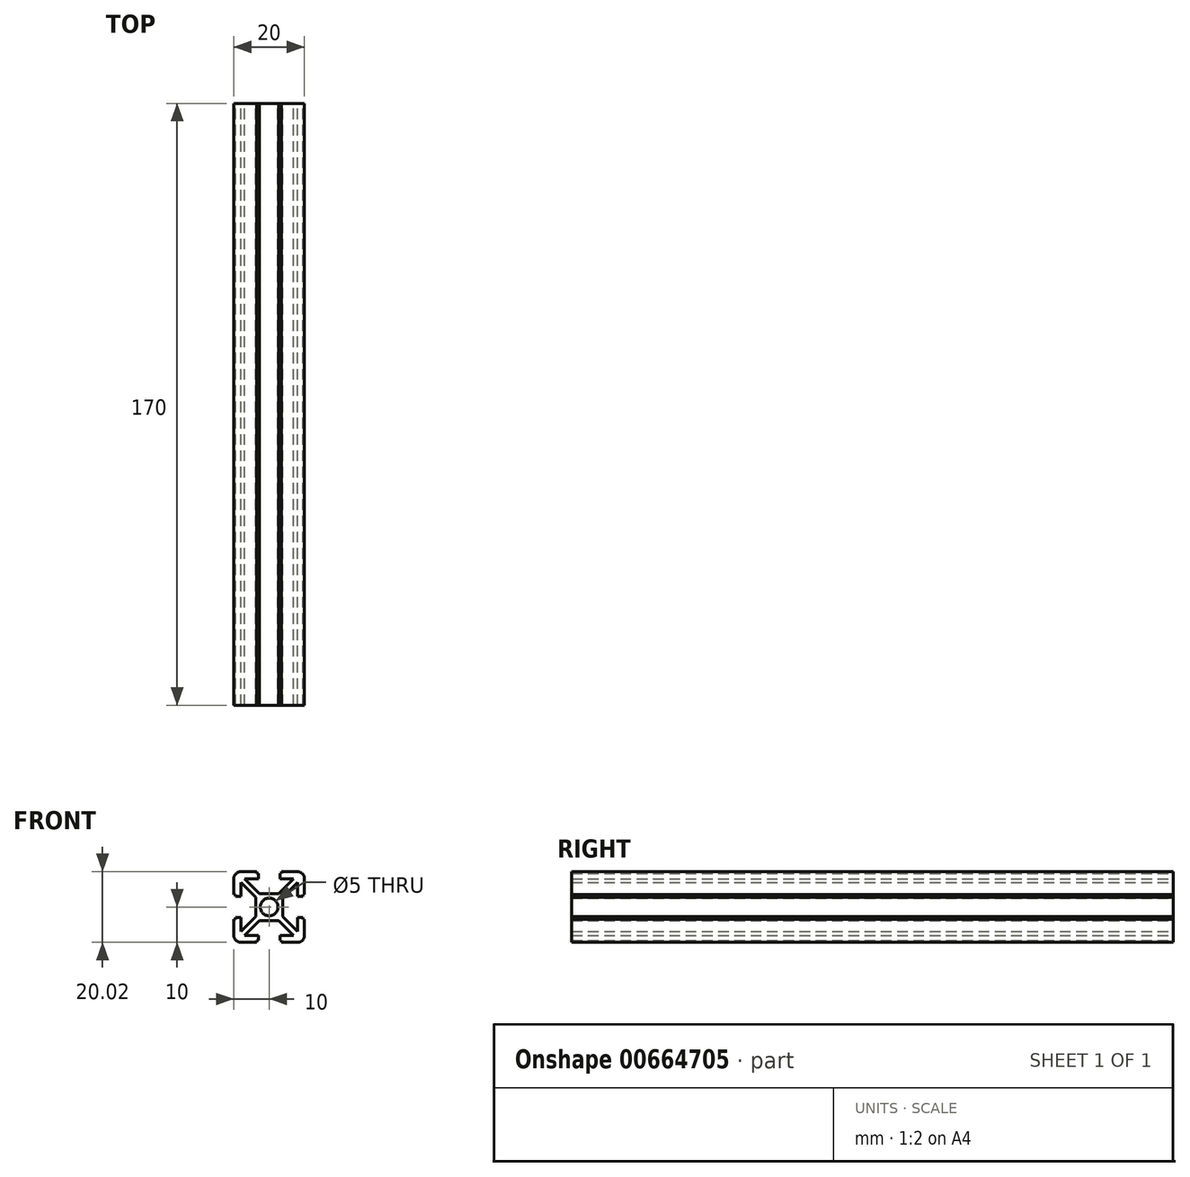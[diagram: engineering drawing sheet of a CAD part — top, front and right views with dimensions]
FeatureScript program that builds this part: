
annotation { "Feature Type Name" : "Feature", "Feature Type Description" : "" }
export const myFeature = defineFeature(function(context is Context, id is Id, definition is map)
    precondition{}
    {
        {
            var Q0;
            Q0=qCreatedBy(makeId("Front.planeOp"),FACE);
            var sketch = newSketch(context, id + "F0", { "sketchPlane" : qUnion([Q0])});
            skPoint(sketch, "E0.middle", {"position": v(10, -10) * mm});
            skPoint(sketch, "E1.visualSharp", {"position": v(0, 0) * mm});
            skArc(sketch, "E1.filletArc", {"start": v(2, 0) * mm, "mid": v(0.59, -0.59) * mm, "end": v(0, -2) * mm});
            skPoint(sketch, "E2.visualSharp", {"position": v(20, 0) * mm});
            skArc(sketch, "E2.filletArc", {"start": v(20, -2) * mm, "mid": v(19.41, -0.59) * mm, "end": v(18, 0) * mm});
            skPoint(sketch, "E3.visualSharp", {"position": v(20, -20) * mm});
            skArc(sketch, "E3.filletArc", {"start": v(18, -20) * mm, "mid": v(19.41, -19.41) * mm, "end": v(20, -18) * mm});
            skArc(sketch, "E4.filletArc", {"start": v(0, -18) * mm, "mid": v(0.59, -19.41) * mm, "end": v(2, -20) * mm});
            skLineSegment(sketch, "E5", {"start": v(2, 0) * mm, "end": v(6.5, 0) * mm});
            skLineSegment(sketch, "E6", {"start": v(6.5, 0) * mm, "end": v(6.5, -0.5) * mm});
            skLineSegment(sketch, "E7", {"start": v(13.02, -0.5) * mm, "end": v(13.5, -0.5) * mm});
            skLineSegment(sketch, "E8", {"start": v(13.5, 0.02) * mm, "end": v(18, 0) * mm});
            skLineSegment(sketch, "E9", {"start": v(20, -2) * mm, "end": v(20, -6.5) * mm});
            skLineSegment(sketch, "E10", {"start": v(20, -6.5) * mm, "end": v(19.5, -6.5) * mm});
            skLineSegment(sketch, "E11", {"start": v(19.5, -6.5) * mm, "end": v(19.5, -7) * mm});
            skLineSegment(sketch, "E12", {"start": v(13.83, -7.25) * mm, "end": v(13.83, -12.77) * mm});
            skLineSegment(sketch, "E13", {"start": v(19.53, -12.98) * mm, "end": v(19.54, -13.46) * mm});
            skLineSegment(sketch, "E14", {"start": v(20, -13.46) * mm, "end": v(20, -18) * mm});
            skLineSegment(sketch, "E15", {"start": v(18, -20) * mm, "end": v(13.5, -20) * mm});
            skLineSegment(sketch, "E16", {"start": v(13.5, -20) * mm, "end": v(13.5, -19.5) * mm});
            skLineSegment(sketch, "E17", {"start": v(12.74, -13.8) * mm, "end": v(7.26, -13.8) * mm});
            skLineSegment(sketch, "E18", {"start": v(7, -19.5) * mm, "end": v(6.5, -19.5) * mm});
            skLineSegment(sketch, "E19", {"start": v(6.5, -19.5) * mm, "end": v(6.5, -20) * mm});
            skLineSegment(sketch, "E20", {"start": v(6.5, -20) * mm, "end": v(2, -20) * mm});
            skLineSegment(sketch, "E21", {"start": v(0, -18) * mm, "end": v(0, -13.5) * mm});
            skLineSegment(sketch, "E22", {"start": v(6.2, -12.74) * mm, "end": v(6.2, -7.26) * mm});
            skLineSegment(sketch, "E23", {"start": v(0, -6.49) * mm, "end": v(0, -2) * mm});
            skLineSegment(sketch, "E24", {"start": v(7, -19.5) * mm, "end": v(7, -18) * mm});
            skLineSegment(sketch, "E25", {"start": v(13.02, -19.5) * mm, "end": v(13.02, -18) * mm});
            skLineSegment(sketch, "E26", {"start": v(13.02, -18) * mm, "end": v(16.94, -18) * mm});
            skLineSegment(sketch, "E27", {"start": v(7, -0.5) * mm, "end": v(7, -2) * mm});
            skLineSegment(sketch, "E28", {"start": v(7, -2) * mm, "end": v(3.06, -2) * mm});
            skLineSegment(sketch, "E29", {"start": v(3.06, -2) * mm, "end": v(7.26, -6.2) * mm});
            skLineSegment(sketch, "E30", {"start": v(12.74, -6.2) * mm, "end": v(16.94, -2) * mm});
            skLineSegment(sketch, "E31", {"start": v(16.94, -2) * mm, "end": v(13.02, -2) * mm});
            skLineSegment(sketch, "E32", {"start": v(19.53, -12.98) * mm, "end": v(18, -12.98) * mm});
            skLineSegment(sketch, "E33", {"start": v(18, -12.98) * mm, "end": v(18, -16.94) * mm});
            skLineSegment(sketch, "E34", {"start": v(18, -16.94) * mm, "end": v(13.83, -12.77) * mm});
            skLineSegment(sketch, "E35", {"start": v(13.83, -7.25) * mm, "end": v(18, -3.06) * mm});
            skLineSegment(sketch, "E36", {"start": v(18, -3.06) * mm, "end": v(18, -7) * mm});
            skLineSegment(sketch, "E37", {"start": v(18, -7) * mm, "end": v(19.5, -7) * mm});
            skLineSegment(sketch, "E38", {"start": v(13.5, -19.5) * mm, "end": v(13.02, -19.5) * mm});
            skLineSegment(sketch, "E39", {"start": v(16.94, -18) * mm, "end": v(12.74, -13.8) * mm});
            skLineSegment(sketch, "E40", {"start": v(7.26, -13.8) * mm, "end": v(3.06, -18) * mm});
            skLineSegment(sketch, "E41", {"start": v(3.06, -18) * mm, "end": v(7, -18) * mm});
            skLineSegment(sketch, "E42", {"start": v(7, -18) * mm, "end": v(7, -19.5) * mm});
            skLineSegment(sketch, "E43", {"start": v(0.5, -6.49) * mm, "end": v(0.5, -7) * mm});
            skLineSegment(sketch, "E44", {"start": v(0.5, -7) * mm, "end": v(2, -7) * mm});
            skLineSegment(sketch, "E45", {"start": v(2, -7) * mm, "end": v(2, -3.08) * mm});
            skLineSegment(sketch, "E46", {"start": v(2, -3.08) * mm, "end": v(6.2, -7.26) * mm});
            skLineSegment(sketch, "E47", {"start": v(6.2, -12.74) * mm, "end": v(2, -16.94) * mm});
            skLineSegment(sketch, "E48", {"start": v(2, -16.94) * mm, "end": v(2, -13) * mm});
            skLineSegment(sketch, "E49", {"start": v(2, -13) * mm, "end": v(0.5, -13) * mm});
            skLineSegment(sketch, "E50", {"start": v(0.5, -13) * mm, "end": v(0.5, -13.5) * mm});
            skLineSegment(sketch, "E51", {"start": v(0.5, -13.5) * mm, "end": v(0, -13.5) * mm});
            skCircle(sketch, "E52", {"center": v(10, -10) * mm, "radius": 2.5 * mm});
            skLineSegment(sketch, "E53", {"start": v(13.5, 0.02) * mm, "end": v(13.5, -0.5) * mm});
            skLineSegment(sketch, "E54", {"start": v(6.5, -0.5) * mm, "end": v(7, -0.5) * mm});
            skLineSegment(sketch, "E55", {"start": v(13.02, -0.5) * mm, "end": v(13.02, -2) * mm});
            skLineSegment(sketch, "E56", {"start": v(7.26, -6.2) * mm, "end": v(12.74, -6.2) * mm});
            skLineSegment(sketch, "E57", {"start": v(0, -6.49) * mm, "end": v(0.5, -6.49) * mm});
            skLineSegment(sketch, "E58", {"start": v(19.54, -13.46) * mm, "end": v(20, -13.46) * mm});
            skSolve(sketch);
        }
        {
            assignVariable(context, id + "F1", {"name" : "L", "anyValue" : 170 * mm});
        }
        {
            var Q0;
            Q0 = qSketchRegion(id + "F0", true);
            extrude(context, id + "F2", {"entities" : qUnion([Q0]), "depth" : getVariable(context, 'L'), "offsetDistance" : 25 * mm});
        }
    });
